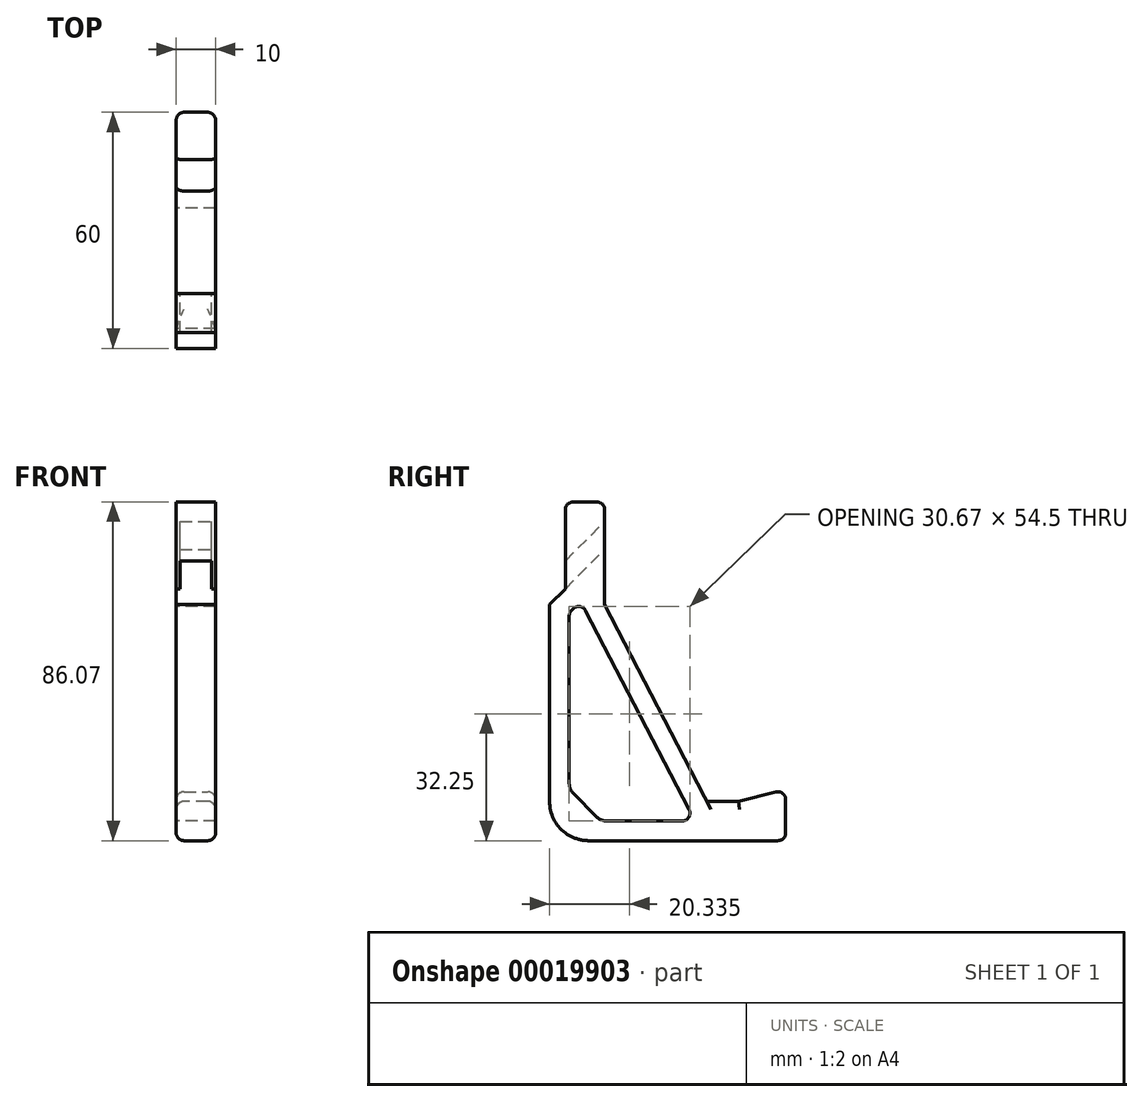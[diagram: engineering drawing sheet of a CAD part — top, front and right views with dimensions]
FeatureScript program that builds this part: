
annotation { "Feature Type Name" : "Feature", "Feature Type Description" : "" }
export const myFeature = defineFeature(function(context is Context, id is Id, definition is map)
    precondition{}
    {
        {
            var Q0;
            Q0=qCreatedBy(makeId("Right.planeOp"),FACE);
            var sketch = newSketch(context, id + "F0", { "sketchPlane" : qUnion([Q0])});
            skLineSegment(sketch, "E0", {"start": v(0, 60) * mm, "end": v(0, 10) * mm});
            skLineSegment(sketch, "E1", {"start": v(10, 0) * mm, "end": v(60, 0) * mm});
            skLineSegment(sketch, "E2", {"start": v(60, 0) * mm, "end": v(60, 13) * mm});
            skLineSegment(sketch, "E3", {"start": v(40, 10) * mm, "end": v(14, 60) * mm});
            skLineSegment(sketch, "E4", {"start": v(14, 60) * mm, "end": v(14, 86.07) * mm});
            skLineSegment(sketch, "E5", {"start": v(14, 86.07) * mm, "end": v(4, 86.07) * mm});
            skLineSegment(sketch, "E6", {"start": v(4, 86.07) * mm, "end": v(4, 64) * mm});
            skLineSegment(sketch, "E7", {"start": v(4, 64) * mm, "end": v(14, 74) * mm});
            skLineSegment(sketch, "E8", {"start": v(4, 71.07) * mm, "end": v(14, 81.07) * mm});
            skLineSegment(sketch, "E9", {"start": v(4, 64) * mm, "end": v(0, 60) * mm});
            skLineSegment(sketch, "E10", {"start": v(40, 10) * mm, "end": v(48, 10) * mm});
            skLineSegment(sketch, "E11", {"start": v(48, 10) * mm, "end": v(60, 13) * mm});
            skPoint(sketch, "E12.visualSharp", {"position": v(0, 0) * mm});
            skArc(sketch, "E12.filletArc", {"start": v(0, 10) * mm, "mid": v(2.93, 2.93) * mm, "end": v(10, 0) * mm});
            skLineSegment(sketch, "E13", {"start": v(9.18, 58.43) * mm, "end": v(35.44, 7.92) * mm});
            skLineSegment(sketch, "E14", {"start": v(33.67, 5) * mm, "end": v(14.66, 5) * mm});
            skLineSegment(sketch, "E15", {"start": v(11.83, 6.17) * mm, "end": v(6.17, 11.83) * mm});
            skLineSegment(sketch, "E16", {"start": v(5, 14.66) * mm, "end": v(5, 57.1) * mm});
            skLineSegment(sketch, "E17", {"start": v(5.59, 58.51) * mm, "end": v(6, 58.92) * mm});
            skPoint(sketch, "E18.visualSharp", {"position": v(36.96, 5) * mm});
            skArc(sketch, "E18.filletArc", {"start": v(33.67, 5) * mm, "mid": v(35.38, 5.96) * mm, "end": v(35.44, 7.92) * mm});
            skPoint(sketch, "E19.visualSharp", {"position": v(7.92, 60.85) * mm});
            skArc(sketch, "E19.filletArc", {"start": v(9.18, 58.43) * mm, "mid": v(7.71, 59.48) * mm, "end": v(6, 58.92) * mm});
            skPoint(sketch, "E20.visualSharp", {"position": v(5, 57.93) * mm});
            skArc(sketch, "E20.filletArc", {"start": v(5.59, 58.51) * mm, "mid": v(5.15, 57.87) * mm, "end": v(5, 57.1) * mm});
            skPoint(sketch, "E21.visualSharp", {"position": v(13, 5) * mm});
            skArc(sketch, "E21.filletArc", {"start": v(11.83, 6.17) * mm, "mid": v(13.13, 5.3) * mm, "end": v(14.66, 5) * mm});
            skPoint(sketch, "E22.visualSharp", {"position": v(5, 13) * mm});
            skArc(sketch, "E22.filletArc", {"start": v(5, 14.66) * mm, "mid": v(5.3, 13.13) * mm, "end": v(6.17, 11.83) * mm});
            skSolve(sketch);
        }
        {
            var Q0;
            Q0 = qSketchRegion(id + "F0", true);
            extrude(context, id + "F1", {"entities" : qUnion([Q0]), "endBound" : BoundingType.SYMMETRIC, "depth" : 10 * mm});
        }
        {
            var Q0;
            {var subQ1=sQuery(id+"F0.wireOp",EDGE,"E7");Q0=makeQuery(id+"F0.imprint","IMPRINT",FACE,{"disambiguationData":[TD([[makeQuery(id+"F0.imprint","IMPRINT",EDGE,{"derivedFrom":subQ1}),1.0]])]});}
            extrude(context, id + "F2", {"entities" : qUnion([Q0]), "operationType" : NewBodyOperationType.REMOVE, "endBound" : BoundingType.SYMMETRIC, "oppositeDirection" : true, "depth" : 8 * mm});
        }
        {
            var Q0;
            Q0=makeQuery(id+"F1.opExtrude","CAP_EDGE",EDGE,{"disambiguationData":[OSD([sQuery(id+"F0.wireOp",EDGE,"E11")])],"isStart":false});
            var Q1;
            Q1=makeQuery(id+"F1.opExtrude","CAP_EDGE",EDGE,{"disambiguationData":[OSD([sQuery(id+"F0.wireOp",EDGE,"E10")])],"isStart":false});
            var Q2;
            Q2=makeQuery(id+"F1.opExtrude","CAP_EDGE",EDGE,{"disambiguationData":[OSD([sQuery(id+"F0.wireOp",EDGE,"E10")])],"isStart":true});
            var Q3;
            Q3=makeQuery(id+"F1.opExtrude","CAP_EDGE",EDGE,{"disambiguationData":[OSD([sQuery(id+"F0.wireOp",EDGE,"E11")])],"isStart":true});
            var Q4;
            Q4=makeQuery(id+"F1.opExtrude","SWEPT_EDGE",EDGE,{"disambiguationData":[OSD([sQuery(id+"F0.wireOp",EDGE,"E2"),sQuery(id+"F0.wireOp",EDGE,"E11")])]});
            var Q5;
            Q5=makeQuery(id+"F1.opExtrude","CAP_EDGE",EDGE,{"disambiguationData":[OSD([sQuery(id+"F0.wireOp",EDGE,"E2")])],"isStart":false});
            var Q6;
            Q6=makeQuery(id+"F1.opExtrude","CAP_EDGE",EDGE,{"disambiguationData":[OSD([sQuery(id+"F0.wireOp",EDGE,"E2")])],"isStart":true});
            var Q7;
            Q7=makeQuery(id+"F1.opExtrude","SWEPT_EDGE",EDGE,{"disambiguationData":[OSD([sQuery(id+"F0.wireOp",EDGE,"E5"),sQuery(id+"F0.wireOp",EDGE,"E6")])]});
            var Q8;
            Q8=makeQuery(id+"F1.opExtrude","SWEPT_EDGE",EDGE,{"disambiguationData":[OSD([sQuery(id+"F0.wireOp",EDGE,"E4"),sQuery(id+"F0.wireOp",EDGE,"E5")])]});
            var Q9;
            Q9=makeQuery(id+"F1.opExtrude","CAP_EDGE",EDGE,{"disambiguationData":[OSD([sQuery(id+"F0.wireOp",EDGE,"E1")])],"isStart":true});
            var Q10;
            Q10=makeQuery(id+"F1.opExtrude","CAP_EDGE",EDGE,{"disambiguationData":[OSD([sQuery(id+"F0.wireOp",EDGE,"E1")])],"isStart":false});
            var Q11;
            Q11=makeQuery(id+"F1.opExtrude","SWEPT_EDGE",EDGE,{"disambiguationData":[OSD([sQuery(id+"F0.wireOp",EDGE,"E1"),sQuery(id+"F0.wireOp",EDGE,"E2")])]});
            fillet(context, id + "F3", {"entities" : qUnion([Q0, Q1, Q2, Q3, Q4, Q5, Q6, Q7, Q8, Q9, Q10, Q11]), "radius" : 2 * mm, "allowEdgeOverflow" : false});
        }
    });
